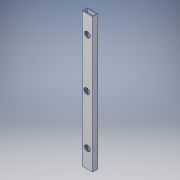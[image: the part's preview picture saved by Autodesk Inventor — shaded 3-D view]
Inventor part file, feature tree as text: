
AUTODESK INVENTOR PART (.ipt)
format: ipt  version: 2018 (Build 220112000, 112)  size: 125,952 bytes
history: native  units: in
note: dims shown in document units (in); Inventor stores cm internally (conversion verified against a paired STEP export)
features: extrude x3, sketch x3
ambient origin geometry x8: Origin, YZ Plane, XZ Plane, XY Plane, X Axis, Y Axis, Z Axis, Center Point
bodies: Solid1 (feature_tree)
feature tree (6):
  extrude  "Extrusion1"  Depth=1.0in
  extrude  "Extrusion2"  Depth=0.125in
  extrude  "Extrusion3"  Depth=0.125in
  sketch  "Sketch1"  dims[d0=2.0in d1=1.0in]
  sketch  "Sketch2"  dims[d2=0.125in d3=0.125in]
  sketch  "Sketch3"  dims[d4=0.125in d5=0.125in d6=26.0in d7=0.0in d9=1.0in d10=0.0in d11=0.125in d12=3.5in d13=3.5in d14=1.125in d15=1.0in d16=0.0in]
